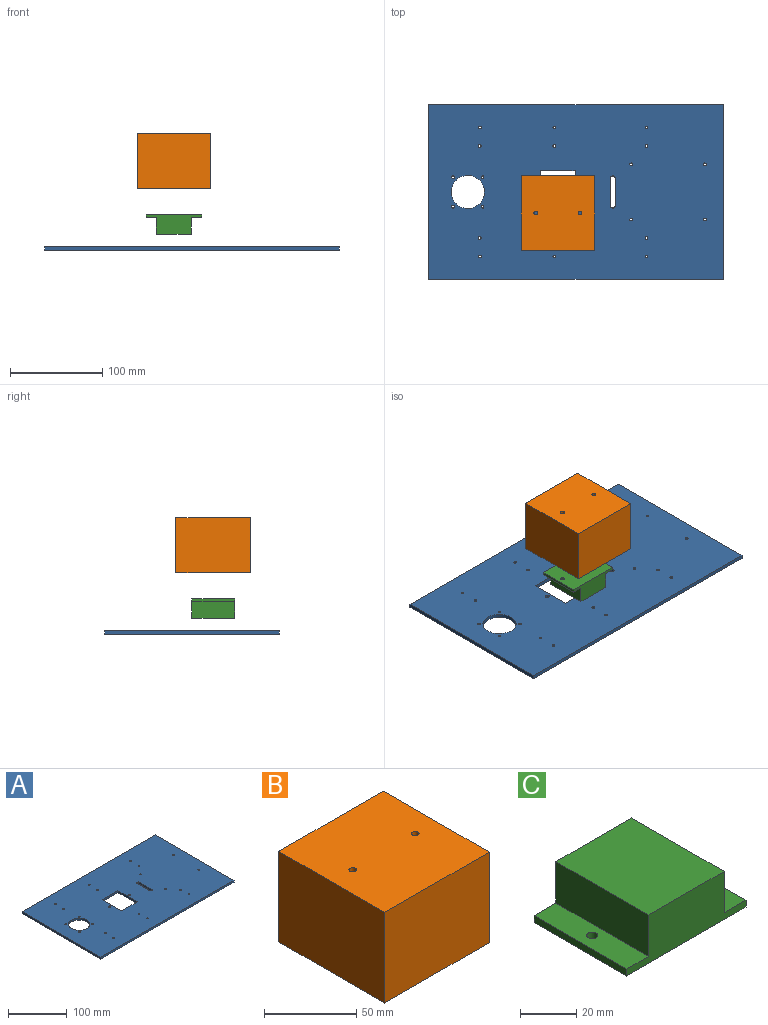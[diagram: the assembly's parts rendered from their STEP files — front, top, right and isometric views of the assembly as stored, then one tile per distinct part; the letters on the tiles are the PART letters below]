
ASSEMBLY  parts=3 mates=2
PART A: 37 faces, bbox 320x190x4 mm
  f0: cylinder r=2.5mm len=5mm, axis (0,0,-1), area 31.4mm2, adj f1,f9,f13,f14
  f1: plane 30x4mm, normal (-1,0,0), area 120mm2, adj f0,f2,f13,f14
  f2: cylinder r=2.5mm len=5mm, axis (0,0,-1), area 31.4mm2, adj f1,f9,f13,f14
  f3: plane 46.5x4mm, normal (1,0,0), area 186mm2, adj f4,f10,f13,f14
  f4: plane 38x4mm, normal (0,-1,0), area 152mm2, adj f3,f5,f13,f14
  f5: plane 46.5x4mm, normal (-1,0,0), area 186mm2, adj f4,f10,f13,f14
  f6: plane 190x4mm, normal (-1,0,0), area 760mm2, adj f7,f11,f13,f14
  f7: plane 320x4mm, normal (0,-1,0), area 1280mm2, adj f6,f8,f13,f14
  f8: plane 190x4mm, normal (1,0,0), area 760mm2, adj f7,f11,f13,f14
  f9: plane 30x4mm, normal (1,0,0), area 120mm2, adj f0,f2,f13,f14
  f10: plane 38x4mm, normal (0,1,0), area 152mm2, adj f3,f5,f13,f14
  f11: plane 320x4mm, normal (0,1,0), area 1280mm2, adj f6,f8,f13,f14
  f12: cylinder r=18mm len=36mm, axis (0,0,-1), area 452.4mm2, adj f13,f14
  f13: plane 320x190mm, normal (0,0,1), area 57679mm2, adj f0,f1,f2,f3,f4,f5,f6,f7
  f14: plane 320x190mm, normal (0,0,-1), area 57679mm2, adj f0,f1,f2,f3,f4,f5,f6,f7
  f15: cylinder r=1.5mm len=4mm, axis (0,0,1), area 37.7mm2, adj f13,f14
  f16: cylinder r=1.5mm len=4mm, axis (0,0,1), area 37.7mm2, adj f13,f14
  f17: cylinder r=1.5mm len=4mm, axis (0,0,1), area 37.7mm2, adj f13,f14
  f18: cylinder r=1.5mm len=4mm, axis (0,0,1), area 37.7mm2, adj f13,f14
  f19: cylinder r=1.5mm len=4mm, axis (0,0,1), area 37.7mm2, adj f13,f14
  f20: cylinder r=1.5mm len=4mm, axis (0,0,1), area 37.7mm2, adj f13,f14
  f21: cylinder r=1.5mm len=4mm, axis (0,0,1), area 37.7mm2, adj f13,f14
  f22: cylinder r=1.5mm len=4mm, axis (0,0,1), area 37.7mm2, adj f13,f14
  f23: cylinder r=1.5mm len=4mm, axis (0,0,1), area 37.7mm2, adj f13,f14
  f24: cylinder r=1.5mm len=4mm, axis (0,0,1), area 37.7mm2, adj f13,f14
  f25: cylinder r=1.5mm len=4mm, axis (0,0,1), area 37.7mm2, adj f13,f14
  f26: cylinder r=1.5mm len=4mm, axis (0,0,1), area 37.7mm2, adj f13,f14
  f27: cylinder r=1.5mm len=4mm, axis (0,0,1), area 37.7mm2, adj f13,f14
  f28: cylinder r=1.5mm len=4mm, axis (0,0,1), area 37.7mm2, adj f13,f14
  f29: cylinder r=1.5mm len=4mm, axis (0,0,1), area 37.7mm2, adj f13,f14
  f30: cylinder r=1.5mm len=4mm, axis (0,0,1), area 37.7mm2, adj f13,f14
  f31: cylinder r=2mm len=4mm, axis (0,0,1), area 50.3mm2, adj f13,f14
  f32: cylinder r=2mm len=4mm, axis (0,0,1), area 50.3mm2, adj f13,f14
  f33: cylinder r=1.5mm len=4mm, axis (0,0,1), area 37.7mm2, adj f13,f14
  f34: cylinder r=1.5mm len=4mm, axis (0,0,1), area 37.7mm2, adj f13,f14
  f35: cylinder r=1.5mm len=4mm, axis (0,0,1), area 37.7mm2, adj f13,f14
  f36: cylinder r=1.5mm len=4mm, axis (0,0,1), area 37.7mm2, adj f13,f14
PART B: 8 faces, bbox 80x81x60 mm
  f0: plane 80x60mm, normal (0,1,0), area 4800mm2, adj f1,f3,f4,f5
  f1: plane 81x60mm, normal (-1,0,0), area 4860mm2, adj f0,f2,f4,f5
  f2: plane 80x60mm, normal (0,-1,0), area 4800mm2, adj f1,f3,f4,f5
  f3: plane 81x60mm, normal (1,0,0), area 4860mm2, adj f0,f2,f4,f5
  f4: plane 81x80mm, normal (0,0,1), area 6454.9mm2, adj f0,f1,f2,f3,f6,f7
  f5: plane 81x80mm, normal (0,0,-1), area 6454.9mm2, adj f0,f1,f2,f3,f6,f7
  f6: cylinder r=2mm len=60mm, axis (0,0,-1), area 754mm2, adj f4,f5
  f7: cylinder r=2mm len=60mm, axis (0,0,-1), area 754mm2, adj f4,f5
PART C: 12 faces, bbox 60x46.5x21 mm
  f0: plane 46.5x11mm, normal (0,0,1), area 498.9mm2, adj f1,f3,f4,f8,f10
  f1: plane 60x21mm, normal (0,1,0), area 864mm2, adj f0,f2,f4,f5,f6,f7,f8,f9
  f2: plane 46.5x3mm, normal (-1,0,0), area 139.5mm2, adj f1,f3,f5,f6
  f3: plane 60x21mm, normal (0,-1,0), area 864mm2, adj f0,f2,f4,f5,f6,f7,f8,f9
  f4: plane 46.5x3mm, normal (1,0,0), area 139.5mm2, adj f0,f1,f3,f6
  f5: plane 46.5x11mm, normal (0,0,1), area 498.9mm2, adj f1,f2,f3,f7,f11
  f6: plane 60x46.5mm, normal (0,0,-1), area 2764.9mm2, adj f1,f2,f3,f4,f10,f11
  f7: plane 46.5x18mm, normal (-1,0,0), area 837mm2, adj f1,f3,f5,f9
  f8: plane 46.5x18mm, normal (1,0,0), area 837mm2, adj f0,f1,f3,f9
  f9: plane 46.5x38mm, normal (0,0,1), area 1767mm2, adj f1,f3,f7,f8
  f10: cylinder r=2mm len=4mm, axis (0,0,1), area 37.7mm2, adj f0,f6
  f11: cylinder r=2mm len=4mm, axis (0,0,1), area 37.7mm2, adj f5,f6
PLACE A t=(46.46,-94.22,-47.21)mm fixed
PLACE B t=(146.8,18.25,19.73)mm
PLACE C rot(axis=(1,0,0),180deg) t=(156.8,-45.5,-8.6)mm
MATE cylindrical B.f6 <-> C.f10  axis (0,0,-1) through (210.8,-22.25,19.73)mm
MATE cylindrical B.f7 <-> C.f11  axis (0,0,-1) through (162.8,-22.25,19.73)mm
